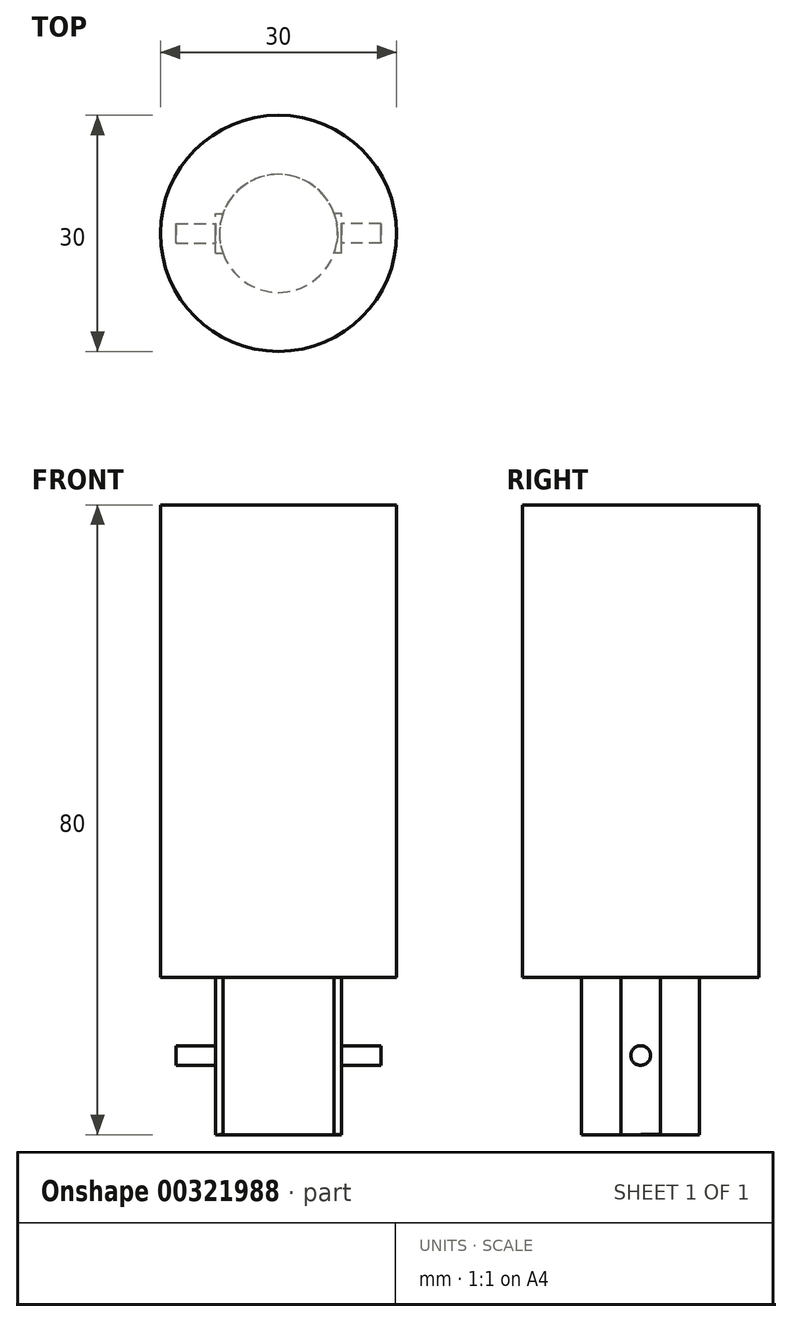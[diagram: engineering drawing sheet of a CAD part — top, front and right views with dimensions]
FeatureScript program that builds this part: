
annotation { "Feature Type Name" : "Feature", "Feature Type Description" : "" }
export const myFeature = defineFeature(function(context is Context, id is Id, definition is map)
    precondition{}
    {
        {
            var Q0;
            Q0=qCreatedBy(makeId("Top.planeOp"),FACE);
            var sketch = newSketch(context, id + "F0", { "sketchPlane" : qUnion([Q0])});
            skCircle(sketch, "E0", {"center": v(0, 0) * mm, "radius": 15 * mm});
            skSolve(sketch);
        }
        {
            var Q0;
            Q0 = qSketchRegion(id + "F0", true);
            extrude(context, id + "F1", {"entities" : qUnion([Q0]), "depth" : 60 * mm});
        }
        {
            var Q0;
            Q0=qCreatedBy(makeId("Top.planeOp"),FACE);
            var sketch = newSketch(context, id + "F2", { "sketchPlane" : qUnion([Q0])});
            skCircle(sketch, "E1", {"center": v(0, 0) * mm, "radius": 7.5 * mm});
            skSolve(sketch);
        }
        {
            var Q0;
            Q0 = qSketchRegion(id + "F2", true);
            extrude(context, id + "F3", {"entities" : qUnion([Q0]), "operationType" : NewBodyOperationType.ADD, "oppositeDirection" : true, "depth" : 20 * mm});
        }
        {
            var Q0;
            Q0=qCreatedBy(makeId("Right.planeOp"),FACE);
            cPlane(context, id + "F4", {"entities" : qUnion([Q0]), "cplaneType" : CPlaneType.OFFSET, "offset" : 7 * mm, "width" : 150 * mm, "height" : 150 * mm});
        }
        {
            var Q0;
            Q0=qCreatedBy(id+"F4.planeOp",FACE);
            var sketch = newSketch(context, id + "F5", { "sketchPlane" : qUnion([Q0])});
            skLineSegment(sketch, "E2", {"start": v(-2.5, -20) * mm, "end": v(-2.5, 0) * mm});
            skLineSegment(sketch, "E3", {"start": v(-2.5, 0) * mm, "end": v(2.5, 0) * mm});
            skLineSegment(sketch, "E4", {"start": v(2.5, 0) * mm, "end": v(2.5, -19.89) * mm});
            skLineSegment(sketch, "E5", {"start": v(2.5, -19.89) * mm, "end": v(-2.5, -20) * mm});
            skSolve(sketch);
        }
        {
            var Q0;
            Q0 = qSketchRegion(id + "F5", true);
            extrude(context, id + "F6", {"entities" : qUnion([Q0]), "operationType" : NewBodyOperationType.ADD, "depth" : 1 * mm});
        }
        {
            var Q0;
            Q0=makeQuery(id+"F6.opExtrude","CAP_FACE",FACE,{"disambiguationData":[OSD([sQuery(id+"F5.wireOp",EDGE,"E2"),sQuery(id+"F5.wireOp",EDGE,"E3"),sQuery(id+"F5.wireOp",EDGE,"E4"),sQuery(id+"F5.wireOp",EDGE,"E5")])],"isStart":false});
            var sketch = newSketch(context, id + "F7", { "sketchPlane" : qUnion([Q0])});
            skLineSegment(sketch, "E6", {"start": v(0, -19.94) * mm, "end": v(0, -9.94) * mm, "construction": true});
            skCircle(sketch, "E7", {"center": v(0, -9.94) * mm, "radius": 1.25 * mm});
            skSolve(sketch);
        }
        {
            var Q0;
            Q0 = qSketchRegion(id + "F7", true);
            extrude(context, id + "F8", {"entities" : qUnion([Q0]), "operationType" : NewBodyOperationType.ADD, "depth" : 5 * mm});
        }
        {
            var Q0;
            Q0=makeQuery(id+"F1.opExtrude","SWEPT_BODY",BODY,{"disambiguationData":[OSD([sQuery(id+"F0.wireOp",EDGE,"E0")])]});
            var Q1;
            Q1=qCreatedBy(makeId("Right.planeOp"),FACE);
            mirror(context, id + "F9", {"operationType" : NewBodyOperationType.ADD, "entities" : qUnion([Q0]), "mirrorPlane" : qUnion([Q1])});
        }
    });
